# Revit family: 24399_BEGA_Revit
name_source: partatom
category: Lighting Fixtures
units: mm (PartAtom-declared; Revit-internal decimal feet)

## family parameters
Cut with Voids When Loaded = Yes
Host = Face
Light Source = Yes
Part Type = Normal
Room Calculation Point = Yes
Round Connector Dimension = Use Diameter
Shared = No

## types (1)
- 24399_BEGA_Revit
    Apparent Load = 0 VA
    BEGA_dummy = No
    BEGA_internal = Yes
    BEGA_internal_off = Yes
    BEGA_internal_on = Yes
    BEGA_internal_structure = Yes
    Bega_IES = Yes
    Color Filter = 16777215
    Colour_rendering_index = CRI > 80
    Colour_temperature = 4000 K
    Default Elevation = 0 mm  [stored 0 ft]
    Description = Ceiling mounted downlight
    Dimming Lamp Color Temperature Shift = <None>
    Fixing_distance = 76 mm
    Fixing_hole = Ø 4,3 mm
    Lamp = LED 8.0 W
    Load_Classification = Lighting
    Logo = BEGA_Logo.png
    Luminaire_luminous_flux = 983 lm
    M_A = No
    M_G = Yes
    M_W = No
    Manufacturer = BEGA
    Material_02 = BEGA_finishes_silver_matt
    Material_03 = BEGA_finishes_white_matt
    Material_06 = BEGA_finishes_stainless_steel_brushed
    Material_09 = BEGA_glass_clear
    Material_11 = BEGA_glass_opal
    Material_15 = BEGA_lighting_medium_matt
    Material_17 = BEGA_reflector
    Model = 24399K4
    Order_number = 24399
    Photometric Web File = 24399K4_BEGA_IES.ies
    Product_data_sheet = www.bega-us.com
    Protection_class = IP 65
    Tilt Angle = 0,00°
    Type Image = 24399.png
    URL = www.bega-us.com
    Update = 2019-07-01T04:00:23
    Voltage = 120 V

note: [stored X ft] marks values corroborated as IEEE doubles in the binary element streams (Revit-internal decimal feet)

## geometry (parser evidence)
native form markers: Sweep x2
no freeform markers — native parametric forms only
